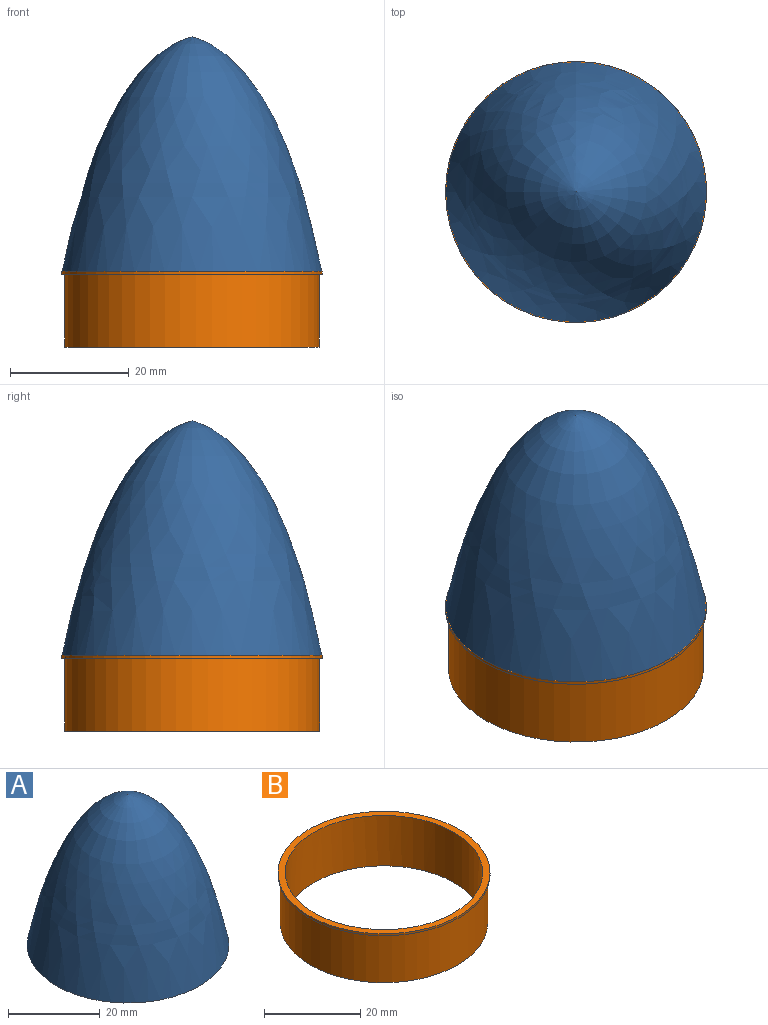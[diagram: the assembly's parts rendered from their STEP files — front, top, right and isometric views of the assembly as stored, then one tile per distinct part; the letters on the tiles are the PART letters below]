
ASSEMBLY  parts=2 mates=1
PART A: 3 faces, bbox 44x44x40 mm
  f0: plane 44x44mm, normal (0,0,-1), area 268.8mm2, adj f1,f2
  f1: revolved ~44x44mm, area 4193.9mm2, adj f0
  f2: revolved ~39.92x39.92mm, area 3535.8mm2, adj f0
PART B: 6 faces, bbox 44x44x12.8 mm
  f0: plane 43x43mm, normal (0,0,-1), area 131.9mm2, adj f1,f5
  f1: cylinder r=21.5mm len=43mm, axis (0,0,-1), area 1660.6mm2, adj f0,f2
  f2: plane 44x44mm, normal (0,0,-1), area 68.3mm2, adj f1,f3
  f3: cylinder r=22mm len=44mm, axis (0,0,-1), area 69.1mm2, adj f2,f4
  f4: plane 44x44mm, normal (0,0,1), area 200.3mm2, adj f3,f5
  f5: cylinder r=20.5mm len=41mm, axis (0,0,1), area 1647.8mm2, adj f0,f4
PLACE A t=(10.4,1.83,21.5)mm
PLACE B t=(10.4,1.83,9.21)mm
MATE fastened A.f0 <-> B.f1  axis (0,0,-1) through (10.4,1.83,21.5)mm
